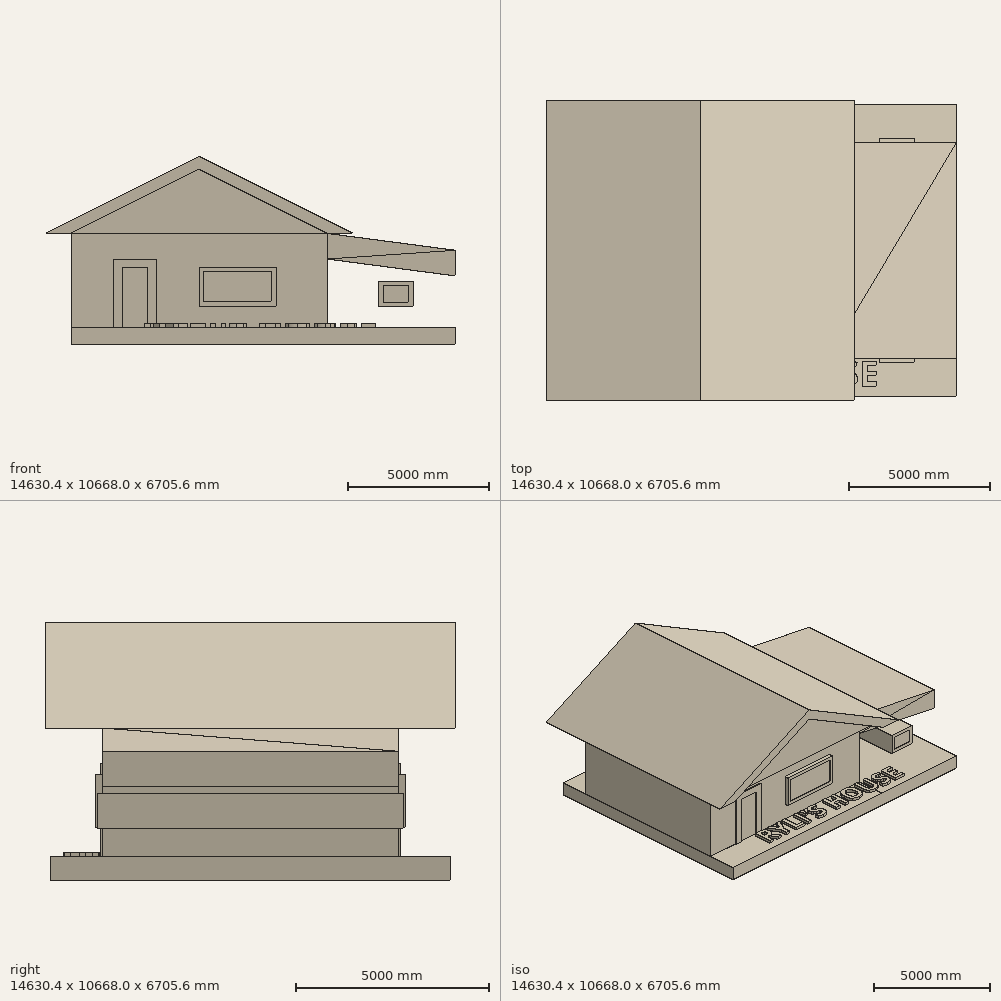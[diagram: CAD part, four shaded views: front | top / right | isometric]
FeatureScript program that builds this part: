
annotation { "Feature Type Name" : "Feature", "Feature Type Description" : "" }
export const myFeature = defineFeature(function(context is Context, id is Id, definition is map)
    precondition{}
    {
        {
            var Q0;
            Q0=qCreatedBy(makeId("Front.planeOp"),FACE);
            var sketch = newSketch(context, id + "F0", { "sketchPlane" : qUnion([Q0])});
            skLineSegment(sketch, "E0", {"start": v(0, 0) * mm, "end": v(0, 3352.8) * mm});
            skLineSegment(sketch, "E1", {"start": v(0, 0) * mm, "end": v(0, -609.6) * mm});
            skLineSegment(sketch, "E2", {"start": v(0, 3352.8) * mm, "end": v(4572, 3352.8) * mm});
            skLineSegment(sketch, "E3", {"start": v(4572, 3352.8) * mm, "end": v(9144, 3352.8) * mm});
            skLineSegment(sketch, "E4", {"start": v(9144, 3352.8) * mm, "end": v(9144, 0) * mm});
            skLineSegment(sketch, "E5", {"start": v(0, 0) * mm, "end": v(4572, 0) * mm});
            skLineSegment(sketch, "E6", {"start": v(4572, 0) * mm, "end": v(9144, 0) * mm});
            skLineSegment(sketch, "E7", {"start": v(0, -609.6) * mm, "end": v(9144, -609.6) * mm});
            skLineSegment(sketch, "E8", {"start": v(9144, -609.6) * mm, "end": v(9144, 0) * mm});
            skLineSegment(sketch, "E9", {"start": v(0, 3352.8) * mm, "end": v(-914.4, 3352.8) * mm});
            skLineSegment(sketch, "E10", {"start": v(4572, 3352.8) * mm, "end": v(4572, 5638.8) * mm});
            skLineSegment(sketch, "E11", {"start": v(0, 3352.8) * mm, "end": v(4572, 5638.8) * mm});
            skLineSegment(sketch, "E12", {"start": v(4572, 5638.8) * mm, "end": v(9144, 3352.8) * mm});
            skLineSegment(sketch, "E13", {"start": v(4572, 5638.8) * mm, "end": v(4572, 6096) * mm});
            skLineSegment(sketch, "E14", {"start": v(4572, 6096) * mm, "end": v(-914.4, 3352.8) * mm});
            skLineSegment(sketch, "E15", {"start": v(4572, 6096) * mm, "end": v(10058.5, 3352.75) * mm});
            skLineSegment(sketch, "E16", {"start": v(9144, 3352.8) * mm, "end": v(10058.5, 3352.75) * mm});
            skLineSegment(sketch, "E17", {"start": v(9144, 3352.8) * mm, "end": v(13716, 2749.53) * mm});
            skLineSegment(sketch, "E18", {"start": v(13716, 2749.53) * mm, "end": v(13716, 6.33) * mm});
            skLineSegment(sketch, "E19", {"start": v(9144, 0) * mm, "end": v(13716, 6.33) * mm});
            skLineSegment(sketch, "E20", {"start": v(9144, -609.6) * mm, "end": v(13716, -609.6) * mm});
            skLineSegment(sketch, "E21", {"start": v(13716, -609.6) * mm, "end": v(13716, 6.33) * mm});
            skLineSegment(sketch, "E22", {"start": v(9144, 3352.8) * mm, "end": v(9144, 2438.4) * mm});
            skLineSegment(sketch, "E23", {"start": v(9144, 2438.4) * mm, "end": v(13716, 1835.13) * mm});
            skLineSegment(sketch, "E24", {"start": v(4572, 0) * mm, "end": v(1828.8, 0) * mm});
            skLineSegment(sketch, "E25", {"start": v(1828.8, 0) * mm, "end": v(1828.8, 2133.6) * mm});
            skLineSegment(sketch, "E26", {"start": v(1828.8, 2133.6) * mm, "end": v(2743.2, 2133.6) * mm});
            skLineSegment(sketch, "E27", {"start": v(2743.2, 2133.6) * mm, "end": v(2743.2, 0) * mm});
            skLineSegment(sketch, "E28", {"start": v(4572, 0) * mm, "end": v(1506.02, 0) * mm});
            skLineSegment(sketch, "E29", {"start": v(1506.02, 0) * mm, "end": v(1506.02, 2438.4) * mm});
            skLineSegment(sketch, "E30", {"start": v(1506.02, 2438.4) * mm, "end": v(3030.02, 2438.4) * mm});
            skLineSegment(sketch, "E31", {"start": v(3030.02, 2438.4) * mm, "end": v(3030.02, 0) * mm});
            skLineSegment(sketch, "E32", {"start": v(4572, 2133.6) * mm, "end": v(7315.2, 2133.6) * mm});
            skLineSegment(sketch, "E33", {"start": v(4572, 2133.6) * mm, "end": v(4572, 762) * mm});
            skLineSegment(sketch, "E34", {"start": v(7315.2, 2133.6) * mm, "end": v(7315.2, 762) * mm});
            skLineSegment(sketch, "E35", {"start": v(7315.2, 762) * mm, "end": v(4572, 762) * mm});
            skLineSegment(sketch, "E36.0", {"start": v(4724.4, 1981.2) * mm, "end": v(4724.4, 914.4) * mm});
            skLineSegment(sketch, "E36.1", {"start": v(4724.4, 1981.2) * mm, "end": v(7162.8, 1981.2) * mm});
            skLineSegment(sketch, "E36.2", {"start": v(7162.8, 1981.2) * mm, "end": v(7162.8, 914.4) * mm});
            skLineSegment(sketch, "E36.3", {"start": v(7162.8, 914.4) * mm, "end": v(4724.4, 914.4) * mm});
            skLineSegment(sketch, "E37", {"start": v(10985.66, 1641.84) * mm, "end": v(12204.86, 1641.84) * mm});
            skLineSegment(sketch, "E38", {"start": v(10985.66, 1641.84) * mm, "end": v(10985.66, 727.44) * mm});
            skLineSegment(sketch, "E39", {"start": v(10985.66, 727.44) * mm, "end": v(12204.86, 727.44) * mm});
            skLineSegment(sketch, "E40", {"start": v(12204.86, 727.44) * mm, "end": v(12204.86, 1641.84) * mm});
            skLineSegment(sketch, "E41.0", {"start": v(11138.06, 1489.44) * mm, "end": v(11138.06, 879.84) * mm});
            skLineSegment(sketch, "E41.1", {"start": v(11138.06, 1489.44) * mm, "end": v(12052.46, 1489.44) * mm});
            skLineSegment(sketch, "E41.2", {"start": v(12052.46, 879.84) * mm, "end": v(12052.46, 1489.44) * mm});
            skLineSegment(sketch, "E41.3", {"start": v(11138.06, 879.84) * mm, "end": v(12052.46, 879.84) * mm});
            skText(sketch, "E42", { "text": "Ryli\'s House", "fontName": "OpenSans-Italic.ttf"});
            const initialGuessF0  = {"E42": [1.12336, 7.4091, 1, 0, 1.17575]};
            skSetInitialGuess(sketch, initialGuessF0);
            skSolve(sketch);
        }
        {
            var Q0;
            Q0=makeQuery(id+"F0.imprint","IMPRINT",FACE,{"disambiguationData":[TD([[makeQuery(id+"F0.imprint","IMPRINT",EDGE,{"derivedFrom":sQuery(id+"F0.wireOp",EDGE,"E12")}),1.0]])]});
            var Q1;
            Q1=makeQuery(id+"F0.imprint","IMPRINT",FACE,{"disambiguationData":[TD([[makeQuery(id+"F0.imprint","IMPRINT",EDGE,{"derivedFrom":sQuery(id+"F0.wireOp",EDGE,"E9")}),-1.0]])]});
            extrude(context, id + "F1", {"entities" : qUnion([Q0, Q1]), "endBound" : BoundingType.SYMMETRIC, "depth" : 10668 * mm, "offsetDistance" : 30.48 * mm});
        }
        {
            var Q0;
            Q0=makeQuery(id+"F0.imprint","IMPRINT",FACE,{"disambiguationData":[TD([[makeQuery(id+"F0.imprint","IMPRINT",EDGE,{"derivedFrom":sQuery(id+"F0.wireOp",EDGE,"E2")}),1.0]])]});
            var Q1;
            Q1=makeQuery(id+"F0.imprint","IMPRINT",FACE,{"disambiguationData":[TD([[makeQuery(id+"F0.imprint","IMPRINT",EDGE,{"derivedFrom":sQuery(id+"F0.wireOp",EDGE,"E3")}),1.0]])]});
            extrude(context, id + "F2", {"entities" : qUnion([Q0, Q1]), "operationType" : NewBodyOperationType.ADD, "endBound" : BoundingType.SYMMETRIC, "depth" : 9631.68 * mm, "offsetDistance" : 30.48 * mm});
        }
        {
            var Q0;
            Q0=makeQuery(id+"F0.imprint","IMPRINT",FACE,{"disambiguationData":[TD([[makeQuery(id+"F0.imprint","IMPRINT",EDGE,{"derivedFrom":sQuery(id+"F0.wireOp",EDGE,"E8")}),-1.0]])]});
            var Q1;
            Q1=makeQuery(id+"F0.imprint","IMPRINT",FACE,{"disambiguationData":[TD([[makeQuery(id+"F0.imprint","IMPRINT",EDGE,{"derivedFrom":sQuery(id+"F0.wireOp",EDGE,"E1")}),1.0]])]});
            extrude(context, id + "F3", {"entities" : qUnion([Q0, Q1]), "endBound" : BoundingType.SYMMETRIC, "depth" : 10424.16 * mm, "offsetDistance" : 30.48 * mm});
        }
        {
            var Q0;
            Q0=makeQuery(id+"F0.imprint","IMPRINT",FACE,{"disambiguationData":[TD([[makeQuery(id+"F0.imprint","IMPRINT",EDGE,{"derivedFrom":sQuery(id+"F0.wireOp",EDGE,"E0")}),-1.0]])]});
            extrude(context, id + "F4", {"entities" : qUnion([Q0]), "endBound" : BoundingType.SYMMETRIC, "depth" : 7680.96 * mm, "offsetDistance" : 30.48 * mm});
        }
        {
            var Q0;
            {var subQ0=sQuery(id+"F0.wireOp",EDGE,"E17");Q0=makeQuery(id+"F0.imprint","IMPRINT",FACE,{"disambiguationData":[TD([[makeQuery(id+"F0.imprint","IMPRINT",EDGE,{"derivedFrom":subQ0}),-1.0]])]});}
            extrude(context, id + "F5", {"entities" : qUnion([Q0]), "operationType" : NewBodyOperationType.ADD, "endBound" : BoundingType.SYMMETRIC, "depth" : 7680.96 * mm, "offsetDistance" : 30.48 * mm});
        }
        {
            var Q0;
            {var subQ3=sQuery(id+"F0.wireOp",EDGE,"E25");Q0=makeQuery(id+"F0.imprint","IMPRINT",FACE,{"disambiguationData":[TD([[makeQuery(id+"F0.imprint","IMPRINT",EDGE,{"derivedFrom":subQ3}),1.0]])]});}
            extrude(context, id + "F6", {"entities" : qUnion([Q0]), "endBound" : BoundingType.SYMMETRIC, "depth" : 7802.88 * mm, "offsetDistance" : 30.48 * mm});
        }
        {
            var Q0;
            Q0=makeQuery(id+"F0.imprint","IMPRINT",FACE,{"disambiguationData":[TD([[makeQuery(id+"F0.imprint","IMPRINT",EDGE,{"derivedFrom":sQuery(id+"F0.wireOp",EDGE,"E32")}),-1.0]])]});
            extrude(context, id + "F7", {"entities" : qUnion([Q0]), "operationType" : NewBodyOperationType.ADD, "endBound" : BoundingType.SYMMETRIC, "depth" : 8046.72 * mm, "offsetDistance" : 30.48 * mm});
        }
        {
            var Q0;
            Q0=makeQuery(id+"F0.imprint","IMPRINT",FACE,{"disambiguationData":[TD([[makeQuery(id+"F0.imprint","IMPRINT",EDGE,{"derivedFrom":sQuery(id+"F0.wireOp",EDGE,"E4")}),1.0]])]});
            extrude(context, id + "F8", {"entities" : qUnion([Q0]), "endBound" : BoundingType.SYMMETRIC, "depth" : 7680.96 * mm, "offsetDistance" : 30.48 * mm});
        }
        {
            var Q0;
            Q0=makeQuery(id+"F0.imprint","IMPRINT",FACE,{"disambiguationData":[TD([[makeQuery(id+"F0.imprint","IMPRINT",EDGE,{"derivedFrom":sQuery(id+"F0.wireOp",EDGE,"E36.0")}),1.0]])]});
            extrude(context, id + "F9", {"entities" : qUnion([Q0]), "endBound" : BoundingType.SYMMETRIC, "depth" : 7985.76 * mm, "offsetDistance" : 30.48 * mm});
        }
        {
            var Q0;
            {var subQ0=sQuery(id+"F0.wireOp",EDGE,"E25");Q0=makeQuery(id+"F0.imprint","IMPRINT",FACE,{"disambiguationData":[TD([[makeQuery(id+"F0.imprint","IMPRINT",EDGE,{"derivedFrom":subQ0}),-1.0]])]});}
            extrude(context, id + "F10", {"entities" : qUnion([Q0]), "endBound" : BoundingType.SYMMETRIC, "depth" : 7680.96 * mm, "offsetDistance" : 30.48 * mm});
        }
        {
            var Q0;
            Q0=makeQuery(id+"F0.imprint","IMPRINT",FACE,{"disambiguationData":[TD([[makeQuery(id+"F0.imprint","IMPRINT",EDGE,{"derivedFrom":sQuery(id+"F0.wireOp",EDGE,"E37")}),-1.0]])]});
            extrude(context, id + "F11", {"entities" : qUnion([Q0]), "endBound" : BoundingType.SYMMETRIC, "depth" : 7985.76 * mm, "offsetDistance" : 30.48 * mm});
        }
        {
            var Q0;
            Q0=makeQuery(id+"F0.imprint","IMPRINT",FACE,{"disambiguationData":[TD([[makeQuery(id+"F0.imprint","IMPRINT",EDGE,{"derivedFrom":sQuery(id+"F0.wireOp",EDGE,"E41.0")}),1.0]])]});
            extrude(context, id + "F12", {"entities" : qUnion([Q0]), "endBound" : BoundingType.SYMMETRIC, "depth" : 7924.8 * mm, "offsetDistance" : 30.48 * mm});
        }
        {
            var Q0;
            Q0=makeQuery(id+"F3.opExtrude","SWEPT_FACE",FACE,{"disambiguationData":[OSD([sQuery(id+"F0.wireOp",EDGE,"E5"),sQuery(id+"F0.wireOp",EDGE,"E6"),sQuery(id+"F0.wireOp",EDGE,"E28")])]});
            var sketch = newSketch(context, id + "F13", { "sketchPlane" : qUnion([Q0])});
            skText(sketch, "E43", { "text": "RYLI\'S HOUSE", "fontName": "OpenSans-Bold.ttf"});
            const initialGuessF13  = {"E43": [2.5206, -4.84906, 1, 0, 0.90694]};
            skSetInitialGuess(sketch, initialGuessF13);
            skSolve(sketch);
        }
        {
            var Q0;
            Q0 = qSketchRegion(id + "F13", true);
            extrude(context, id + "F14", {"entities" : qUnion([Q0]), "operationType" : NewBodyOperationType.ADD, "endBound" : BoundingType.SYMMETRIC, "depth" : 243.84 * mm, "offsetDistance" : 30.48 * mm});
        }
    });
